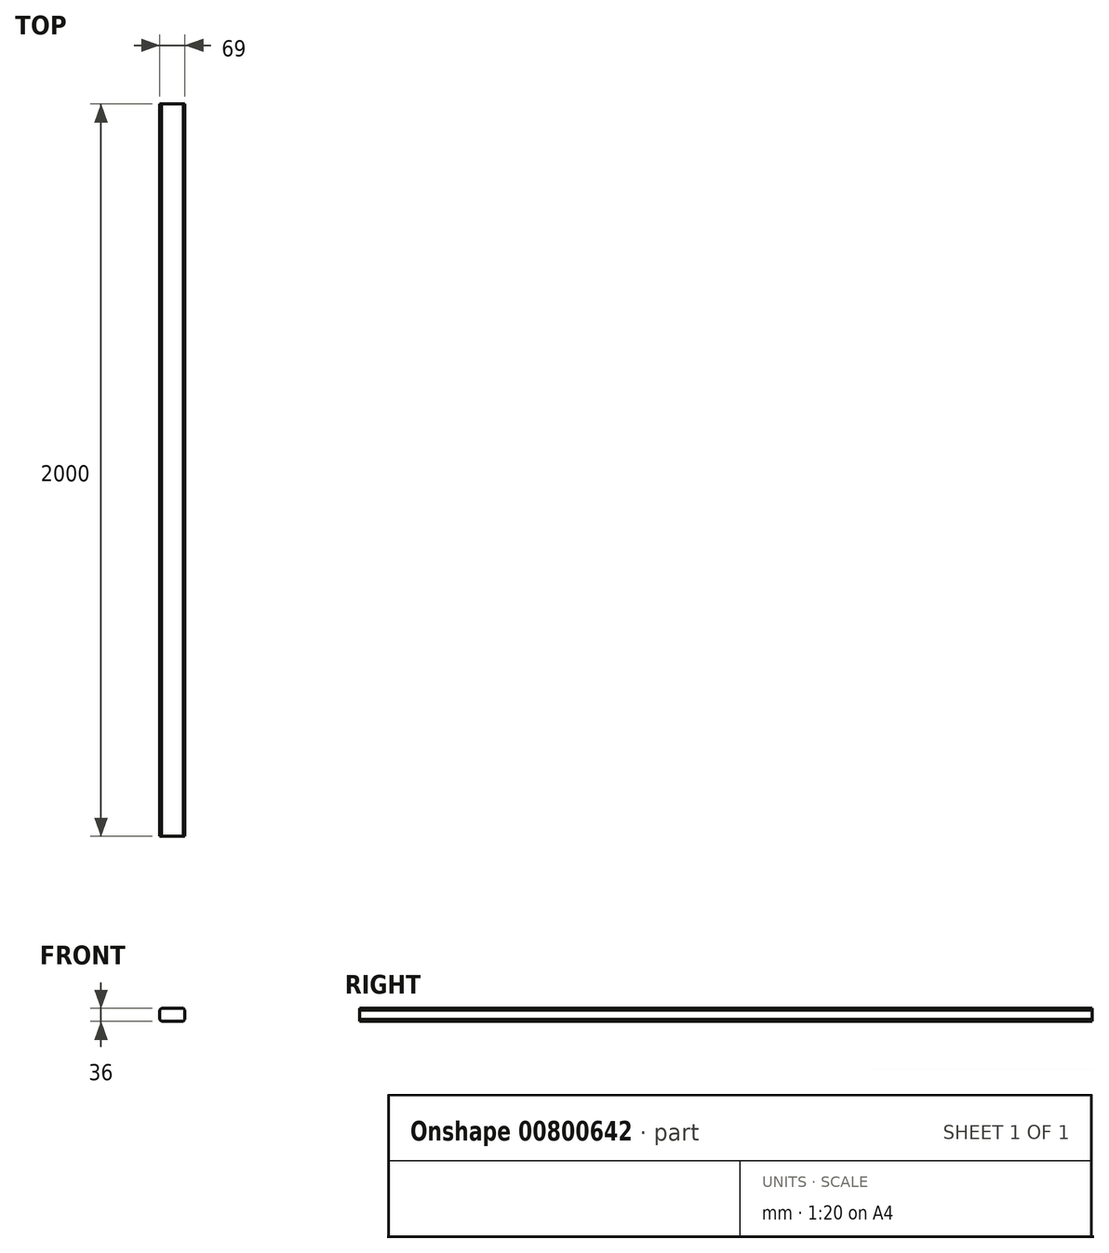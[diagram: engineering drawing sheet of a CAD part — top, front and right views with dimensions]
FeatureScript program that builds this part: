
annotation { "Feature Type Name" : "Feature", "Feature Type Description" : "" }
export const myFeature = defineFeature(function(context is Context, id is Id, definition is map)
    precondition{}
    {
        {
            var Q0;
            Q0=qCreatedBy(makeId("Front.planeOp"),FACE);
            var sketch = newSketch(context, id + "F0", { "sketchPlane" : qUnion([Q0])});
            skLineSegment(sketch, "E0.bottom", {"start": v(34.5, 18) * mm, "end": v(-34.5, 18) * mm});
            skLineSegment(sketch, "E0.top", {"start": v(34.5, -18) * mm, "end": v(-34.5, -18) * mm});
            skLineSegment(sketch, "E0.left", {"start": v(34.5, 18) * mm, "end": v(34.5, -18) * mm});
            skLineSegment(sketch, "E0.right", {"start": v(-34.5, 18) * mm, "end": v(-34.5, -18) * mm});
            skPoint(sketch, "E0.middle", {"position": v(0, 0) * mm});
            skSolve(sketch);
        }
        {
            var Q0;
            Q0=makeQuery(id+"F0.imprint","IMPRINT",FACE,{"disambiguationData":[TD([[makeQuery(id+"F0.imprint","IMPRINT",EDGE,{"derivedFrom":sQuery(id+"F0.wireOp",EDGE,"E0.bottom")}),1.0]])]});
            extrude(context, id + "F1", {"entities" : qUnion([Q0]), "depth" : 2000 * mm, "offsetDistance" : 25 * mm});
        }
        {
            var Q0;
            Q0=makeQuery(id+"F1.opExtrude","SWEPT_EDGE",EDGE,{"disambiguationData":[OSD([sQuery(id+"F0.wireOp",EDGE,"E0.top"),sQuery(id+"F0.wireOp",EDGE,"E0.right")])]});
            var Q1;
            Q1=makeQuery(id+"F1.opExtrude","SWEPT_EDGE",EDGE,{"disambiguationData":[OSD([sQuery(id+"F0.wireOp",EDGE,"E0.bottom"),sQuery(id+"F0.wireOp",EDGE,"E0.right")])]});
            var Q2;
            Q2=makeQuery(id+"F1.opExtrude","SWEPT_EDGE",EDGE,{"disambiguationData":[OSD([sQuery(id+"F0.wireOp",EDGE,"E0.bottom"),sQuery(id+"F0.wireOp",EDGE,"E0.left")])]});
            var Q3;
            Q3=makeQuery(id+"F1.opExtrude","SWEPT_EDGE",EDGE,{"disambiguationData":[OSD([sQuery(id+"F0.wireOp",EDGE,"E0.top"),sQuery(id+"F0.wireOp",EDGE,"E0.left")])]});
            chamfer(context, id + "F2", {"entities" : qUnion([Q0, Q1, Q2, Q3]), "width" : 5 * mm, "tangentPropagation" : true});
        }
    });
